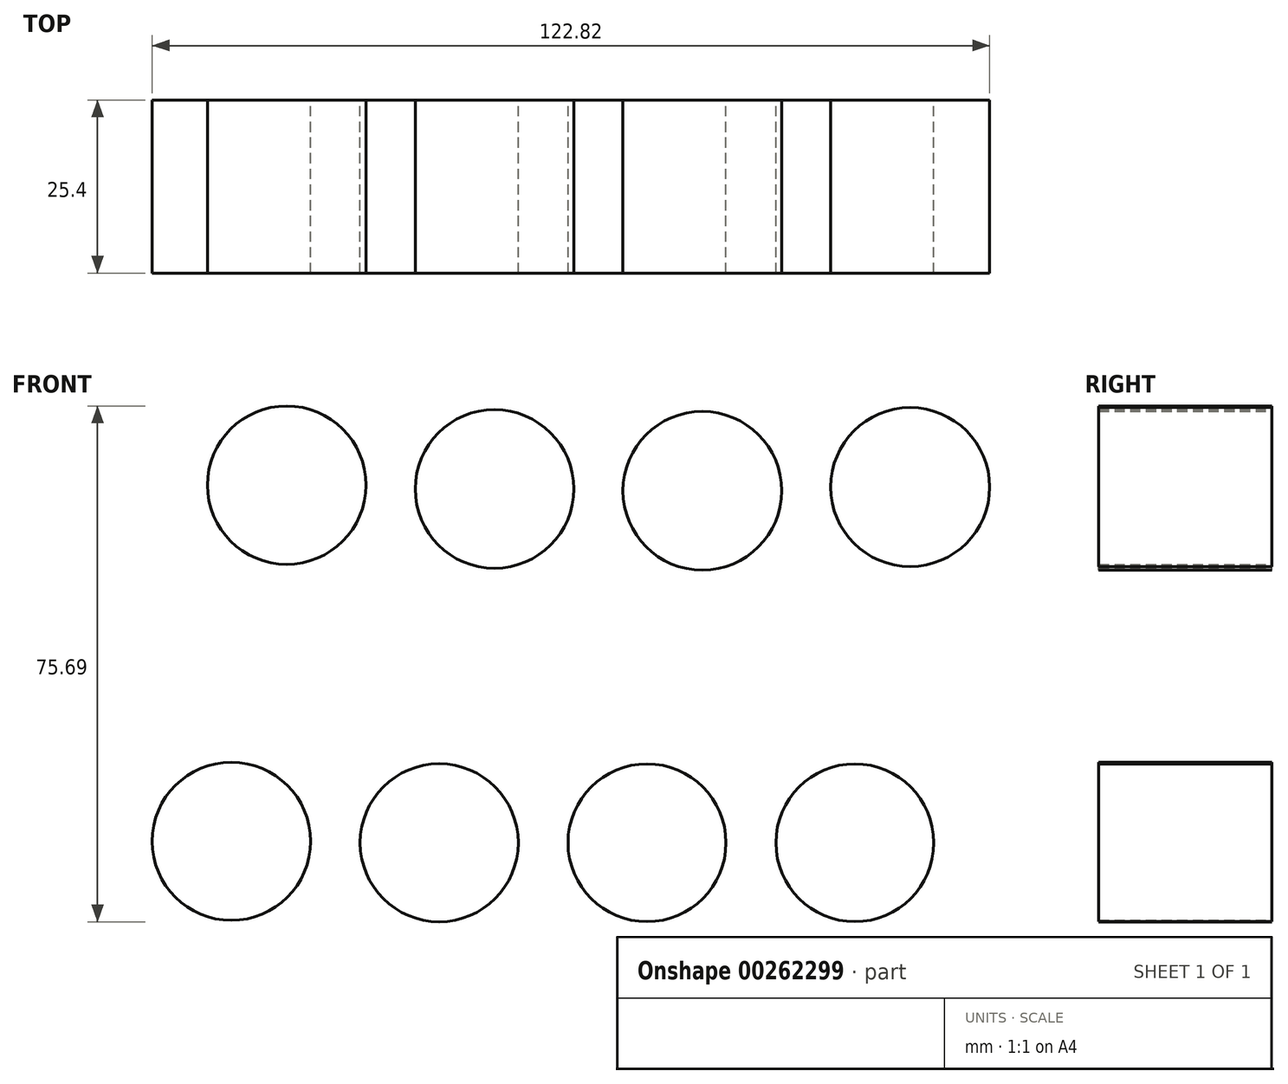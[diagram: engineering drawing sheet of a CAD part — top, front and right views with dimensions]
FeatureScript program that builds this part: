
annotation { "Feature Type Name" : "Feature", "Feature Type Description" : "" }
export const myFeature = defineFeature(function(context is Context, id is Id, definition is map)
    precondition{}
    {
        {
            var Q0;
            Q0=qCreatedBy(makeId("Front.planeOp"),FACE);
            var sketch = newSketch(context, id + "F0", { "sketchPlane" : qUnion([Q0])});
            skCircle(sketch, "E0", {"center": v(-20.94, 32.6) * mm, "radius": 11.63 * mm});
            skCircle(sketch, "E1", {"center": v(9.54, 32.34) * mm, "radius": 11.65 * mm});
            skCircle(sketch, "E2", {"center": v(-51.42, 33.17) * mm, "radius": 11.62 * mm});
            skCircle(sketch, "E3", {"center": v(40.02, 32.89) * mm, "radius": 11.66 * mm});
            skCircle(sketch, "E4", {"center": v(-59.53, -19.1) * mm, "radius": 11.6 * mm});
            skCircle(sketch, "E5", {"center": v(-29.05, -19.3) * mm, "radius": 11.6 * mm});
            skCircle(sketch, "E6", {"center": v(1.43, -19.3) * mm, "radius": 11.58 * mm});
            skCircle(sketch, "E7", {"center": v(31.9, -19.3) * mm, "radius": 11.57 * mm});
            skSolve(sketch);
        }
        {
            var Q0;
            Q0 = qSketchRegion(id + "F0", true);
            extrude(context, id + "F1", {"entities" : qUnion([Q0]), "depth" : 25.4 * mm});
        }
        {
            var Q0;
            Q0 = qSketchRegion(id + "F0", true);
            extrude(context, id + "F2", {"entities" : qUnion([Q0]), "depth" : 25.4 * mm});
        }
    });
